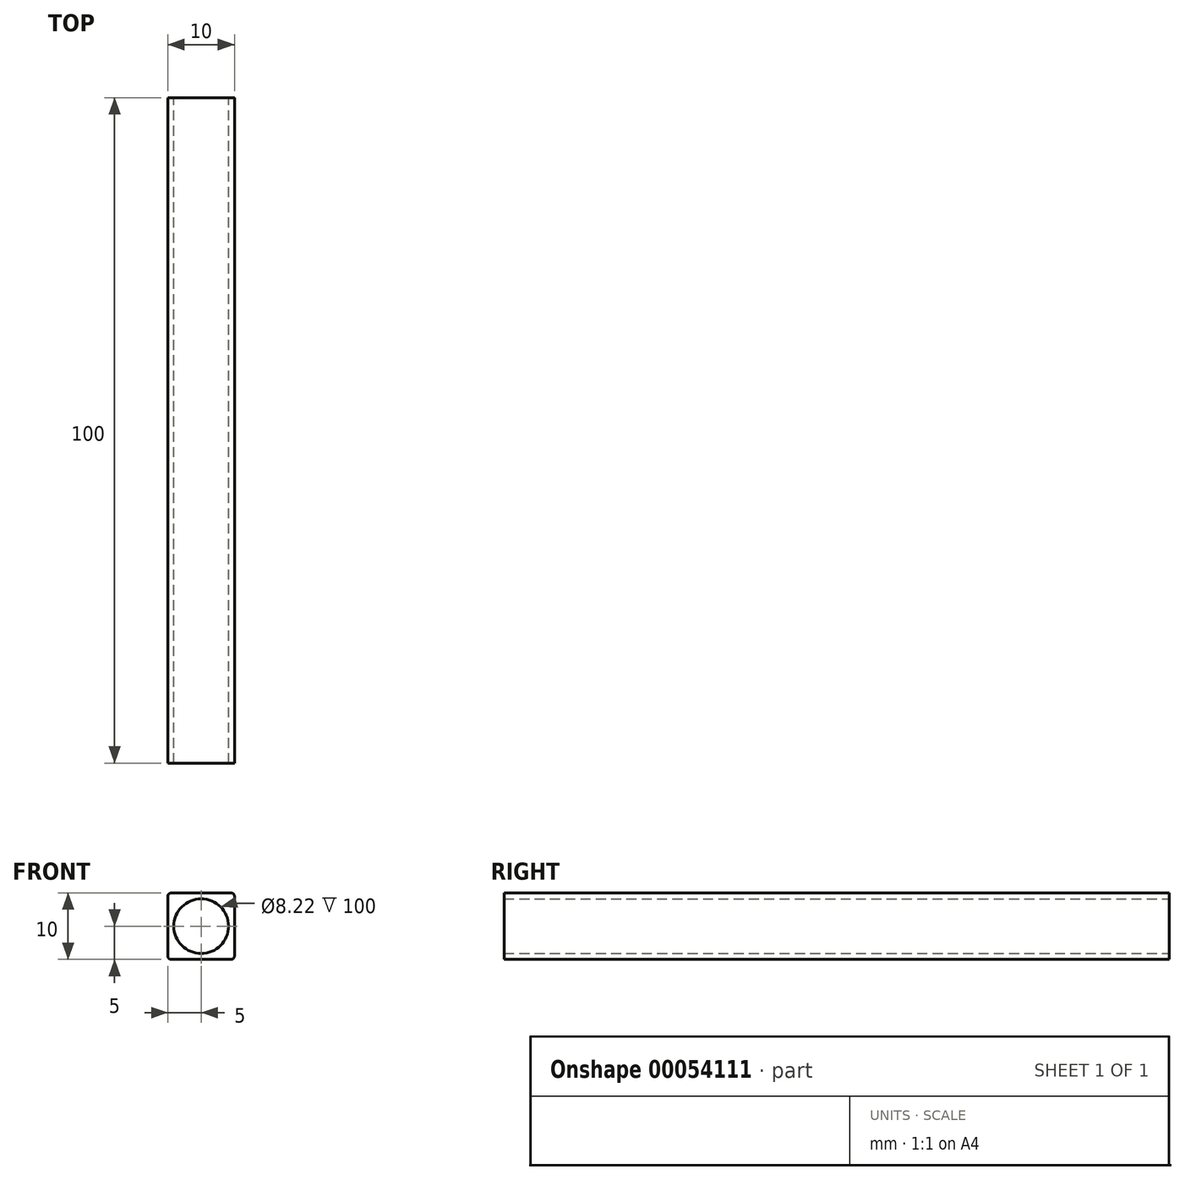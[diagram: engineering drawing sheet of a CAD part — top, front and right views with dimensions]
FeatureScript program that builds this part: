
annotation { "Feature Type Name" : "Feature", "Feature Type Description" : "" }
export const myFeature = defineFeature(function(context is Context, id is Id, definition is map)
    precondition{}
    {
        {
            var Q0;
            Q0=qCreatedBy(makeId("Front.planeOp"),FACE);
            var sketch = newSketch(context, id + "F0", { "sketchPlane" : qUnion([Q0])});
            skLineSegment(sketch, "E0.rect.bottom", {"start": v(5, -5) * mm, "end": v(-5, -5) * mm});
            skLineSegment(sketch, "E0.rect.top", {"start": v(5, 5) * mm, "end": v(-5, 5) * mm});
            skLineSegment(sketch, "E0.rect.left", {"start": v(5, -5) * mm, "end": v(5, 5) * mm});
            skLineSegment(sketch, "E0.rect.right", {"start": v(-5, -5) * mm, "end": v(-5, 5) * mm});
            skPoint(sketch, "E0.rect.middle", {"position": v(0, 0) * mm});
            skCircle(sketch, "E1", {"center": v(0, 0) * mm, "radius": 4.1 * mm});
            skSolve(sketch);
        }
        {
            var Q0;
            Q0=makeQuery(id+"F0.imprint","IMPRINT",FACE,{"disambiguationData":[TD([[makeQuery(id+"F0.imprint","IMPRINT",EDGE,{"derivedFrom":sQuery(id+"F0.wireOp",EDGE,"E0.rect.bottom")}),-1.0]])]});
            extrude(context, id + "F1", {"entities" : qUnion([Q0]), "depth" : 100 * mm});
        }
        {
            var Q0;
            Q0=makeQuery(id+"F1.opExtrude","SWEPT_EDGE",EDGE,{"disambiguationData":[OSD([sQuery(id+"F0.wireOp",EDGE,"E0.rect.top"),sQuery(id+"F0.wireOp",EDGE,"E0.rect.left")])]});
            var Q1;
            Q1=makeQuery(id+"F1.opExtrude","SWEPT_EDGE",EDGE,{"disambiguationData":[OSD([sQuery(id+"F0.wireOp",EDGE,"E0.rect.top"),sQuery(id+"F0.wireOp",EDGE,"E0.rect.right")])]});
            var Q2;
            Q2=makeQuery(id+"F1.opExtrude","SWEPT_EDGE",EDGE,{"disambiguationData":[OSD([sQuery(id+"F0.wireOp",EDGE,"E0.rect.bottom"),sQuery(id+"F0.wireOp",EDGE,"E0.rect.left")])]});
            var Q3;
            Q3=makeQuery(id+"F1.opExtrude","SWEPT_EDGE",EDGE,{"disambiguationData":[OSD([sQuery(id+"F0.wireOp",EDGE,"E0.rect.bottom"),sQuery(id+"F0.wireOp",EDGE,"E0.rect.right")])]});
            fillet(context, id + "F2", {"entities" : qUnion([Q0, Q1, Q2, Q3]), "radius" : .5 * mm, "tangentPropagation" : true, "allowEdgeOverflow" : false});
        }
    });
